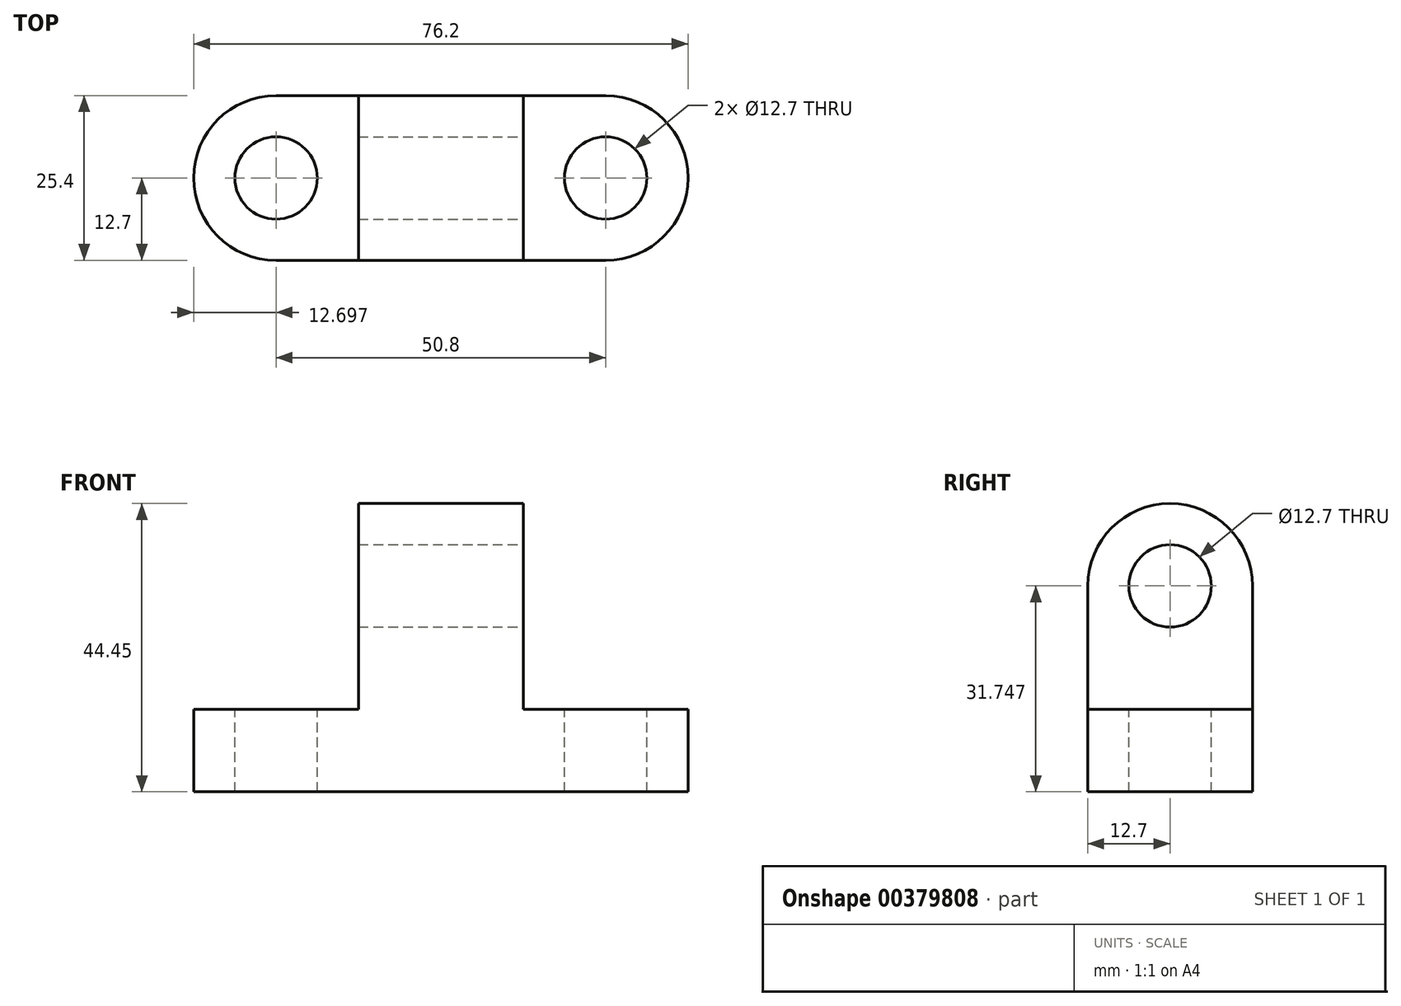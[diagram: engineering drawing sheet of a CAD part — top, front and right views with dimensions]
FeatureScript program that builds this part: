
annotation { "Feature Type Name" : "Feature", "Feature Type Description" : "" }
export const myFeature = defineFeature(function(context is Context, id is Id, definition is map)
    precondition{}
    {
        {
            var Q0;
            Q0=qCreatedBy(makeId("Front.planeOp"),FACE);
            var sketch = newSketch(context, id + "F0", { "sketchPlane" : qUnion([Q0])});
            skLineSegment(sketch, "E0.bottom", {"start": v(-42.74, 25.46) * mm, "end": v(33.46, 25.46) * mm});
            skLineSegment(sketch, "E0.top", {"start": v(-42.74, -19) * mm, "end": v(33.46, -19) * mm});
            skLineSegment(sketch, "E0.left", {"start": v(-42.74, 25.46) * mm, "end": v(-42.74, -19) * mm});
            skLineSegment(sketch, "E0.right", {"start": v(33.46, 25.46) * mm, "end": v(33.46, -19) * mm});
            skLineSegment(sketch, "E1", {"start": v(-17.34, 25.46) * mm, "end": v(-17.34, -6.3) * mm});
            skLineSegment(sketch, "E2", {"start": v(-17.34, -6.3) * mm, "end": v(-42.74, -6.3) * mm});
            skLineSegment(sketch, "E3", {"start": v(8.06, 25.46) * mm, "end": v(8.06, -6.3) * mm});
            skLineSegment(sketch, "E4", {"start": v(8.06, -6.3) * mm, "end": v(33.46, -6.3) * mm});
            skSolve(sketch);
        }
        {
            var Q0;
            {var subQ1=sQuery(id+"F0.wireOp",EDGE,"E0.top");Q0=makeQuery(id+"F0.imprint","IMPRINT",FACE,{"disambiguationData":[TD([[makeQuery(id+"F0.imprint","IMPRINT",EDGE,{"derivedFrom":subQ1}),1.0]])]});}
            extrude(context, id + "F1", {"entities" : qUnion([Q0]), "depth" : 25.4 * mm});
        }
        {
            var Q0;
            Q0=makeQuery(id+"F1.opExtrude","SWEPT_FACE",FACE,{"disambiguationData":[OSD([sQuery(id+"F0.wireOp",EDGE,"E4")])]});
            var sketch = newSketch(context, id + "F2", { "sketchPlane" : qUnion([Q0])});
            skLineSegment(sketch, "E5", {"start": v(20.76, 0) * mm, "end": v(20.76, 0) * mm});
            skLineSegment(sketch, "E6", {"start": v(33.46, -12.7) * mm, "end": v(33.46, -12.7) * mm});
            skLineSegment(sketch, "E7", {"start": v(20.76, -25.4) * mm, "end": v(20.76, -25.4) * mm});
            skPoint(sketch, "E8.visualSharp", {"position": v(33.46, 0) * mm});
            skArc(sketch, "E8.filletArc", {"start": v(33.46, -12.7) * mm, "mid": v(29.74, -3.72) * mm, "end": v(20.76, 0) * mm});
            skPoint(sketch, "E9.visualSharp", {"position": v(33.46, -25.4) * mm});
            skArc(sketch, "E9.filletArc", {"start": v(20.76, -25.4) * mm, "mid": v(29.74, -21.68) * mm, "end": v(33.46, -12.7) * mm});
            skCircle(sketch, "E10", {"center": v(20.76, -12.7) * mm, "radius": 6.35 * mm});
            skSolve(sketch);
        }
        {
            var Q0;
            Q0=makeQuery(id+"F2.imprint","IMPRINT",FACE,{"disambiguationData":[TD([[makeQuery(id+"F2.imprint","IMPRINT",EDGE,{"derivedFrom":sQuery(id+"F2.wireOp",EDGE,"E10")}),1.0]])]});
            var Q1;
            {var subQ0=sQuery(id+"F2.wireOp",EDGE,"E8.filletArc");Q1=makeQuery(id+"F2.imprint","IMPRINT",FACE,{"disambiguationData":[TD([[makeQuery(id+"F2.imprint","IMPRINT",EDGE,{"derivedFrom":subQ0}),-1.0]])]});}
            var Q2;
            {var subQ0=sQuery(id+"F2.wireOp",EDGE,"E9.filletArc");Q2=makeQuery(id+"F2.imprint","IMPRINT",FACE,{"disambiguationData":[TD([[makeQuery(id+"F2.imprint","IMPRINT",EDGE,{"derivedFrom":subQ0}),-1.0]])]});}
            extrude(context, id + "F3", {"entities" : qUnion([Q0, Q1, Q2]), "operationType" : NewBodyOperationType.REMOVE, "oppositeDirection" : true, "depth" : 12.7 * mm});
        }
        {
            var Q0;
            Q0=makeQuery(id+"F1.opExtrude","SWEPT_FACE",FACE,{"disambiguationData":[OSD([sQuery(id+"F0.wireOp",EDGE,"E2")])]});
            var sketch = newSketch(context, id + "F4", { "sketchPlane" : qUnion([Q0])});
            skLineSegment(sketch, "E11", {"start": v(-30.04, 0) * mm, "end": v(-32.24, 0) * mm});
            skLineSegment(sketch, "E12", {"start": v(-42.74, -12.7) * mm, "end": v(-42.74, -12.7) * mm});
            skLineSegment(sketch, "E13", {"start": v(-33.18, -25.4) * mm, "end": v(-30.04, -25.4) * mm});
            skPoint(sketch, "E14.visualSharp", {"position": v(-42.74, 0) * mm});
            skArc(sketch, "E14.filletArc", {"start": v(-30.04, 0) * mm, "mid": v(-39.02, -3.72) * mm, "end": v(-42.74, -12.7) * mm});
            skPoint(sketch, "E15.visualSharp", {"position": v(-42.74, -25.4) * mm});
            skArc(sketch, "E15.filletArc", {"start": v(-42.74, -12.7) * mm, "mid": v(-39.02, -21.68) * mm, "end": v(-30.04, -25.4) * mm});
            skCircle(sketch, "E16", {"center": v(-30.04, -12.7) * mm, "radius": 6.35 * mm});
            skSolve(sketch);
        }
        {
            var Q0;
            {var subQ0=sQuery(id+"F4.wireOp",EDGE,"E13");Q0=makeQuery(id+"F4.imprint","IMPRINT",FACE,{"disambiguationData":[TD([[makeQuery(id+"F4.imprint","IMPRINT",EDGE,{"derivedFrom":subQ0}),-1.0]])]});}
            var Q1;
            Q1=makeQuery(id+"F4.imprint","IMPRINT",FACE,{"disambiguationData":[TD([[makeQuery(id+"F4.imprint","IMPRINT",EDGE,{"derivedFrom":sQuery(id+"F4.wireOp",EDGE,"E16")}),1.0]])]});
            var Q2;
            {var subQ0=sQuery(id+"F4.wireOp",EDGE,"E11");Q2=makeQuery(id+"F4.imprint","IMPRINT",FACE,{"disambiguationData":[TD([[makeQuery(id+"F4.imprint","IMPRINT",EDGE,{"derivedFrom":subQ0}),1.0]])]});}
            extrude(context, id + "F5", {"entities" : qUnion([Q0, Q1, Q2]), "operationType" : NewBodyOperationType.REMOVE, "oppositeDirection" : true, "depth" : 25.4 * mm});
        }
        {
            var Q0;
            Q0=makeQuery(id+"F1.opExtrude","SWEPT_FACE",FACE,{"disambiguationData":[OSD([sQuery(id+"F0.wireOp",EDGE,"E3")])]});
            var sketch = newSketch(context, id + "F6", { "sketchPlane" : qUnion([Q0])});
            skLineSegment(sketch, "E17", {"start": v(-25.4, 12.76) * mm, "end": v(-25.4, 15.1) * mm});
            skLineSegment(sketch, "E18", {"start": v(-12.7, 25.46) * mm, "end": v(-12.7, 25.46) * mm});
            skLineSegment(sketch, "E19", {"start": v(0, 16.7) * mm, "end": v(0, 12.76) * mm});
            skPoint(sketch, "E20.visualSharp", {"position": v(-25.4, 25.46) * mm});
            skArc(sketch, "E20.filletArc", {"start": v(-12.7, 25.46) * mm, "mid": v(-21.68, 21.74) * mm, "end": v(-25.4, 12.76) * mm});
            skPoint(sketch, "E21.visualSharp", {"position": v(0, 25.46) * mm});
            skArc(sketch, "E21.filletArc", {"start": v(0, 12.76) * mm, "mid": v(-3.72, 21.74) * mm, "end": v(-12.7, 25.46) * mm});
            skCircle(sketch, "E22", {"center": v(-12.7, 12.76) * mm, "radius": 6.35 * mm});
            skSolve(sketch);
        }
        {
            var Q0;
            Q0=makeQuery(id+"F6.imprint","IMPRINT",FACE,{"disambiguationData":[TD([[makeQuery(id+"F6.imprint","IMPRINT",EDGE,{"derivedFrom":sQuery(id+"F6.wireOp",EDGE,"E22")}),1.0]])]});
            var Q1;
            {var subQ0=sQuery(id+"F6.wireOp",EDGE,"E19");Q1=makeQuery(id+"F6.imprint","IMPRINT",FACE,{"disambiguationData":[TD([[makeQuery(id+"F6.imprint","IMPRINT",EDGE,{"derivedFrom":subQ0}),-1.0]])]});}
            var Q2;
            {var subQ0=sQuery(id+"F6.wireOp",EDGE,"E17");Q2=makeQuery(id+"F6.imprint","IMPRINT",FACE,{"disambiguationData":[TD([[makeQuery(id+"F6.imprint","IMPRINT",EDGE,{"derivedFrom":subQ0}),1.0]])]});}
            extrude(context, id + "F7", {"entities" : qUnion([Q0, Q1, Q2]), "operationType" : NewBodyOperationType.REMOVE, "oppositeDirection" : true, "depth" : 25.4 * mm});
        }
    });
